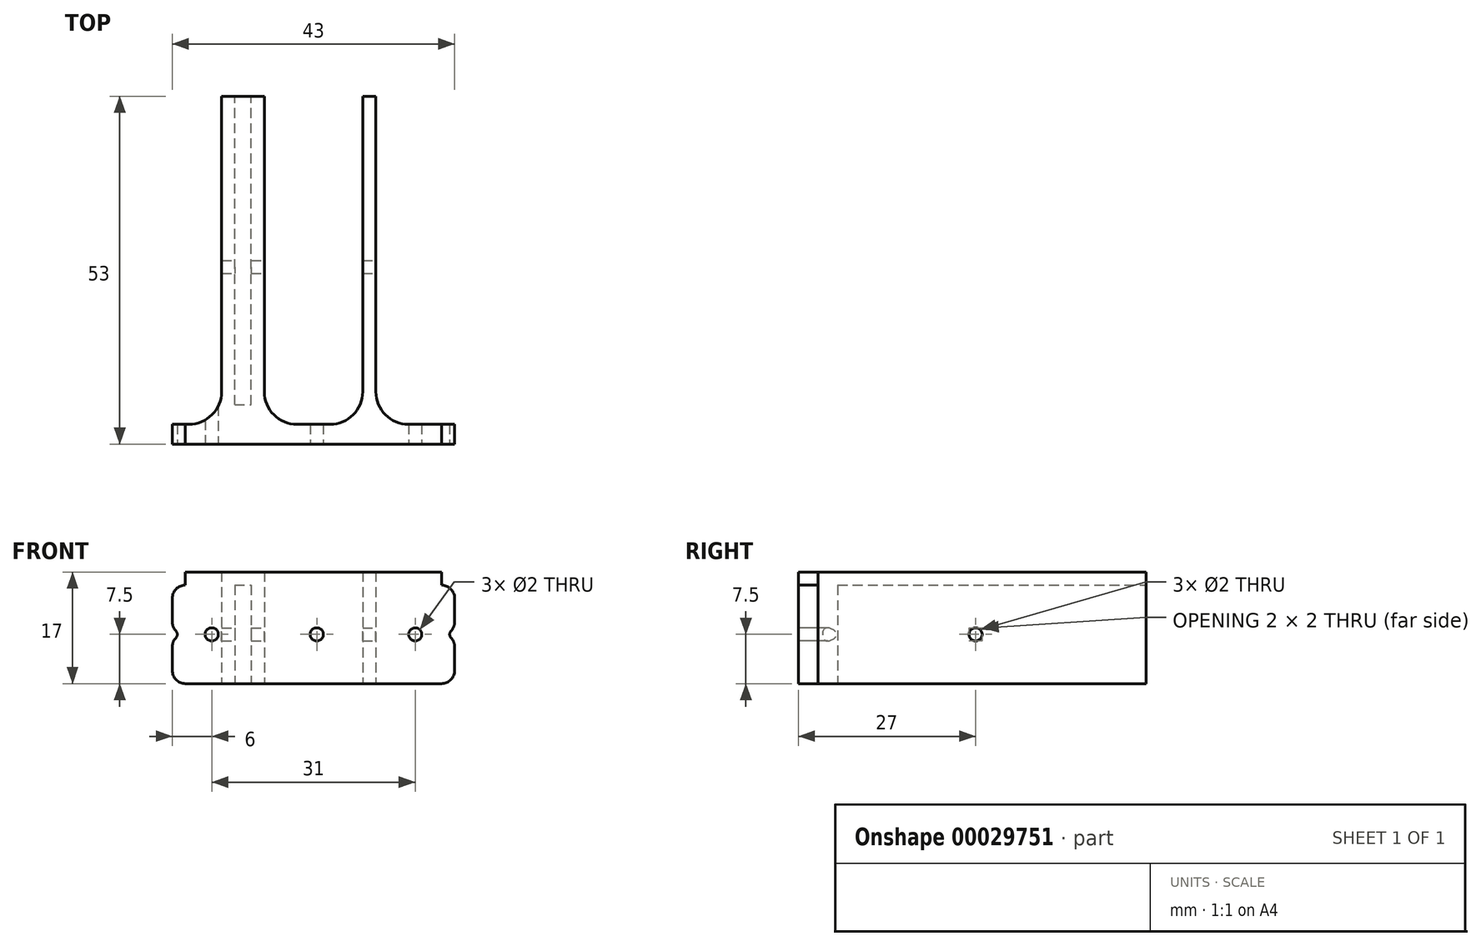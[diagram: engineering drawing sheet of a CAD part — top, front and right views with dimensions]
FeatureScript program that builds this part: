
annotation { "Feature Type Name" : "Feature", "Feature Type Description" : "" }
export const myFeature = defineFeature(function(context is Context, id is Id, definition is map)
    precondition{}
    {
        {
            var Q0;
            Q0=qCreatedBy(makeId("Top.planeOp"),FACE);
            var sketch = newSketch(context, id + "F0", { "sketchPlane" : qUnion([Q0])});
            skLineSegment(sketch, "E0.top", {"start": v(0, 53) * mm, "end": v(-2, 53) * mm});
            skLineSegment(sketch, "E0.left", {"start": v(0, 3) * mm, "end": v(0, 53) * mm});
            skLineSegment(sketch, "E0.right", {"start": v(-19, 6) * mm, "end": v(-19, 53) * mm});
            skLineSegment(sketch, "E1.top", {"start": v(-17, 3) * mm, "end": v(-2, 3) * mm});
            skLineSegment(sketch, "E1.left", {"start": v(-17, 53) * mm, "end": v(-17, 3) * mm});
            skLineSegment(sketch, "E1.right", {"start": v(-2, 53) * mm, "end": v(-2, 3) * mm});
            skLineSegment(sketch, "E2.trimOffspring", {"start": v(-17, 53) * mm, "end": v(-19, 53) * mm});
            skLineSegment(sketch, "E3", {"start": v(-19, 0) * mm, "end": v(0, 0) * mm});
            skLineSegment(sketch, "E4", {"start": v(-19, 0) * mm, "end": v(-31, 0) * mm});
            skLineSegment(sketch, "E5", {"start": v(-31, 0) * mm, "end": v(-31, 3) * mm});
            skLineSegment(sketch, "E6", {"start": v(-31, 3) * mm, "end": v(-23.5, 3) * mm});
            skLineSegment(sketch, "E7", {"start": v(0, 3) * mm, "end": v(12, 3) * mm});
            skLineSegment(sketch, "E8", {"start": v(12, 3) * mm, "end": v(12, 0) * mm});
            skLineSegment(sketch, "E9", {"start": v(12, 0) * mm, "end": v(0, 0) * mm});
            skLineSegment(sketch, "E10", {"start": v(-21.5, 6) * mm, "end": v(-21.5, 53) * mm});
            skLineSegment(sketch, "E11", {"start": v(-21.5, 53) * mm, "end": v(-23.5, 53) * mm});
            skLineSegment(sketch, "E12", {"start": v(-23.5, 53) * mm, "end": v(-23.5, 3) * mm});
            skLineSegment(sketch, "E13", {"start": v(-21.5, 6) * mm, "end": v(-19, 6) * mm});
            skSolve(sketch);
        }
        {
            var Q0;
            Q0=makeQuery(id+"F0.imprint","IMPRINT",FACE,{"disambiguationData":[TD([[makeQuery(id+"F0.imprint","IMPRINT",EDGE,{"derivedFrom":sQuery(id+"F0.wireOp",EDGE,"E0.top")}),1.0]])]});
            extrude(context, id + "F1", {"entities" : qUnion([Q0]), "depth" : 15 * mm});
        }
        {
            var Q0;
            Q0=makeQuery(id+"F1.opExtrude","SWEPT_FACE",FACE,{"disambiguationData":[OSD([sQuery(id+"F0.wireOp",EDGE,"E0.left")])]});
            var sketch = newSketch(context, id + "F2", { "sketchPlane" : qUnion([Q0])});
            skCircle(sketch, "E14", {"center": v(27, 7.5) * mm, "radius": 1 * mm});
            skSolve(sketch);
        }
        {
            var Q0;
            Q0=qSketchRegion(id+"F2",true);
            extrude(context, id + "F3", {"entities" : qUnion([Q0]), "operationType" : NewBodyOperationType.REMOVE, "oppositeDirection" : true, "depth" : 25 * mm});
        }
        {
            var Q0;
            Q0=makeQuery(id+"F1.opExtrude","SWEPT_EDGE",EDGE,{"disambiguationData":[OSD([sQuery(id+"F0.wireOp",EDGE,"E6"),sQuery(id+"F0.wireOp",EDGE,"E12")])]});
            var Q1;
            Q1=makeQuery(id+"F1.opExtrude","SWEPT_EDGE",EDGE,{"disambiguationData":[OSD([sQuery(id+"F0.wireOp",EDGE,"E0.left"),sQuery(id+"F0.wireOp",EDGE,"E7")])]});
            var Q2;
            Q2=makeQuery(id+"F1.opExtrude","SWEPT_EDGE",EDGE,{"disambiguationData":[OSD([sQuery(id+"F0.wireOp",EDGE,"E1.top"),sQuery(id+"F0.wireOp",EDGE,"E1.right")])]});
            var Q3;
            Q3=makeQuery(id+"F1.opExtrude","SWEPT_EDGE",EDGE,{"disambiguationData":[OSD([sQuery(id+"F0.wireOp",EDGE,"E1.top"),sQuery(id+"F0.wireOp",EDGE,"E1.left")])]});
            fillet(context, id + "F4", {"entities" : qUnion([Q0, Q1, Q2, Q3]), "radius" : 5 * mm, "tangentPropagation" : true, "allowEdgeOverflow" : false});
        }
        {
            var Q0;
            Q0=makeQuery(id+"F1.opExtrude","SWEPT_FACE",FACE,{"disambiguationData":[OSD([sQuery(id+"F0.wireOp",EDGE,"E3"),sQuery(id+"F0.wireOp",EDGE,"E4"),sQuery(id+"F0.wireOp",EDGE,"E9")])]});
            var sketch = newSketch(context, id + "F5", { "sketchPlane" : qUnion([Q0])});
            skCircle(sketch, "E15", {"center": v(-9, 7.5) * mm, "radius": 1 * mm});
            skCircle(sketch, "E16", {"center": v(-25, 7.5) * mm, "radius": 1 * mm});
            skCircle(sketch, "E17", {"center": v(6, 7.5) * mm, "radius": 1 * mm});
            skLineSegment(sketch, "E18.0", {"start": v(12, 15) * mm, "end": v(12, 0) * mm});
            skCircle(sketch, "E19", {"center": v(-31, 7.5) * mm, "radius": 0.75 * mm});
            skCircle(sketch, "E20", {"center": v(12, 7.5) * mm, "radius": 0.75 * mm});
            skSolve(sketch);
        }
        {
            var Q0;
            Q0=qSketchRegion(id+"F5",true);
            extrude(context, id + "F6", {"entities" : qUnion([Q0]), "operationType" : NewBodyOperationType.REMOVE, "oppositeDirection" : true, "depth" : 25 * mm});
        }
        {
            var Q0;
            Q0=makeQuery(id+"F6.boolean.opBoolean","INTERSECT",EDGE,{"disambiguationData":[OD(1.0)],"derivedFrom":[makeQuery(id+"F1.opExtrude","SWEPT_FACE",FACE,{"disambiguationData":[OSD([sQuery(id+"F0.wireOp",EDGE,"E5")])]}),makeQuery(id+"F6.opExtrude","SWEPT_FACE",FACE,{"disambiguationData":[OSD([sQuery(id+"F5.wireOp",EDGE,"E19")])]})]});
            var Q1;
            Q1=makeQuery(id+"F6.boolean.opBoolean","INTERSECT",EDGE,{"disambiguationData":[OD(0.0)],"derivedFrom":[makeQuery(id+"F1.opExtrude","SWEPT_FACE",FACE,{"disambiguationData":[OSD([sQuery(id+"F0.wireOp",EDGE,"E5")])]}),makeQuery(id+"F6.opExtrude","SWEPT_FACE",FACE,{"disambiguationData":[OSD([sQuery(id+"F5.wireOp",EDGE,"E19")])]})]});
            var Q2;
            Q2=makeQuery(id+"F6.boolean.opBoolean","INTERSECT",EDGE,{"disambiguationData":[OD(1.0)],"derivedFrom":[makeQuery(id+"F1.opExtrude","SWEPT_FACE",FACE,{"disambiguationData":[OSD([sQuery(id+"F0.wireOp",EDGE,"E8")])]}),makeQuery(id+"F6.opExtrude","SWEPT_FACE",FACE,{"disambiguationData":[OSD([sQuery(id+"F5.wireOp",EDGE,"E20")])]})]});
            var Q3;
            Q3=makeQuery(id+"F6.boolean.opBoolean","INTERSECT",EDGE,{"disambiguationData":[OD(0.0)],"derivedFrom":[makeQuery(id+"F1.opExtrude","SWEPT_FACE",FACE,{"disambiguationData":[OSD([sQuery(id+"F0.wireOp",EDGE,"E8")])]}),makeQuery(id+"F6.opExtrude","SWEPT_FACE",FACE,{"disambiguationData":[OSD([sQuery(id+"F5.wireOp",EDGE,"E20")])]})]});
            var Q4;
            Q4=makeQuery(id+"F1.opExtrude","CAP_EDGE",EDGE,{"disambiguationData":[OSD([sQuery(id+"F0.wireOp",EDGE,"E5")])],"isStart":false});
            var Q5;
            Q5=makeQuery(id+"F1.opExtrude","CAP_EDGE",EDGE,{"disambiguationData":[OSD([sQuery(id+"F0.wireOp",EDGE,"E5")])],"isStart":true});
            var Q6;
            Q6=makeQuery(id+"F1.opExtrude","CAP_EDGE",EDGE,{"disambiguationData":[OSD([sQuery(id+"F0.wireOp",EDGE,"E8")])],"isStart":false});
            var Q7;
            Q7=makeQuery(id+"F1.opExtrude","CAP_EDGE",EDGE,{"disambiguationData":[OSD([sQuery(id+"F0.wireOp",EDGE,"E8")])],"isStart":true});
            fillet(context, id + "F7", {"entities" : qUnion([Q0, Q1, Q2, Q3, Q4, Q5, Q6, Q7]), "radius" : 2 * mm, "tangentPropagation" : true, "allowEdgeOverflow" : false});
        }
        {
            var Q0;
            Q0=makeQuery(id+"F1.opExtrude","CAP_FACE",FACE,{"disambiguationData":[OSD([sQuery(id+"F0.wireOp",EDGE,"E0.top"),sQuery(id+"F0.wireOp",EDGE,"E0.left"),sQuery(id+"F0.wireOp",EDGE,"E0.right"),sQuery(id+"F0.wireOp",EDGE,"E1.top"),sQuery(id+"F0.wireOp",EDGE,"E1.left"),sQuery(id+"F0.wireOp",EDGE,"E1.right"),sQuery(id+"F0.wireOp",EDGE,"E2.trimOffspring"),sQuery(id+"F0.wireOp",EDGE,"E3"),sQuery(id+"F0.wireOp",EDGE,"E4"),sQuery(id+"F0.wireOp",EDGE,"E5"),sQuery(id+"F0.wireOp",EDGE,"E6"),sQuery(id+"F0.wireOp",EDGE,"E7"),sQuery(id+"F0.wireOp",EDGE,"E8"),sQuery(id+"F0.wireOp",EDGE,"E9"),sQuery(id+"F0.wireOp",EDGE,"E10"),sQuery(id+"F0.wireOp",EDGE,"E11"),sQuery(id+"F0.wireOp",EDGE,"E12"),sQuery(id+"F0.wireOp",EDGE,"E13")])],"isStart":false});
            var sketch = newSketch(context, id + "F8", { "sketchPlane" : qUnion([Q0])});
            skPoint(sketch, "E21.orphan", {"position": v(10, 0) * mm});
            skLineSegment(sketch, "E22", {"start": v(-29, 3) * mm, "end": v(-28.5, 3) * mm});
            skLineSegment(sketch, "E23.0", {"start": v(-23.5, 53) * mm, "end": v(-23.5, 8) * mm});
            skArc(sketch, "E24.0", {"start": v(-23.5, 8) * mm, "mid": v(-24.96, 4.46) * mm, "end": v(-28.5, 3) * mm});
            skLineSegment(sketch, "E25.0", {"start": v(-29, 3) * mm, "end": v(-29, 0) * mm});
            skLineSegment(sketch, "E26.0", {"start": v(10, 0) * mm, "end": v(-29, 0) * mm});
            skLineSegment(sketch, "E27.0", {"start": v(-17, 53) * mm, "end": v(-17, 8) * mm});
            skArc(sketch, "E28.0", {"start": v(-12, 3) * mm, "mid": v(-15.54, 4.46) * mm, "end": v(-17, 8) * mm});
            skLineSegment(sketch, "E29", {"start": v(-12, 3) * mm, "end": v(-12, 0) * mm});
            skLineSegment(sketch, "E30", {"start": v(-23.5, 53) * mm, "end": v(-17, 53) * mm});
            skSolve(sketch);
        }
        {
            var Q0;
            Q0=makeQuery(id+"F8.imprint","IMPRINT",FACE,{"disambiguationData":[TD([[makeQuery(id+"F8.imprint","IMPRINT",EDGE,{"derivedFrom":sQuery(id+"F8.wireOp",EDGE,"E22")}),-1.0]])]});
            extrude(context, id + "F9", {"entities" : qUnion([Q0]), "operationType" : NewBodyOperationType.ADD, "depth" : 2 * mm});
        }
        {
            var Q0;
            {var subQ1=makeQuery(id+"F1.opExtrude","CAP_EDGE",EDGE,{"disambiguationData":[OSD([sQuery(id+"F0.wireOp",EDGE,"E0.right")])],"isStart":false});Q0=makeQuery(id+"F8.imprint","IMPRINT",FACE,{"disambiguationData":[TD([[makeQuery(id+"F8.imprint","IMPRINT",EDGE,{"derivedFrom":subQ1}),1.0]])]});}
            extrude(context, id + "F10", {"entities" : qUnion([Q0]), "operationType" : NewBodyOperationType.ADD, "depth" : 2 * mm});
        }
        {
            var Q0;
            Q0=makeQuery(id+"F1.opExtrude","CAP_FACE",FACE,{"disambiguationData":[OSD([sQuery(id+"F0.wireOp",EDGE,"E0.top"),sQuery(id+"F0.wireOp",EDGE,"E0.left"),sQuery(id+"F0.wireOp",EDGE,"E0.right"),sQuery(id+"F0.wireOp",EDGE,"E1.top"),sQuery(id+"F0.wireOp",EDGE,"E1.left"),sQuery(id+"F0.wireOp",EDGE,"E1.right"),sQuery(id+"F0.wireOp",EDGE,"E2.trimOffspring"),sQuery(id+"F0.wireOp",EDGE,"E3"),sQuery(id+"F0.wireOp",EDGE,"E4"),sQuery(id+"F0.wireOp",EDGE,"E5"),sQuery(id+"F0.wireOp",EDGE,"E6"),sQuery(id+"F0.wireOp",EDGE,"E7"),sQuery(id+"F0.wireOp",EDGE,"E8"),sQuery(id+"F0.wireOp",EDGE,"E9"),sQuery(id+"F0.wireOp",EDGE,"E10"),sQuery(id+"F0.wireOp",EDGE,"E11"),sQuery(id+"F0.wireOp",EDGE,"E12"),sQuery(id+"F0.wireOp",EDGE,"E13")])],"isStart":false});
            extrude(context, id + "F11", {"entities" : qUnion([Q0]), "operationType" : NewBodyOperationType.ADD, "depth" : 2 * mm});
        }
    });
